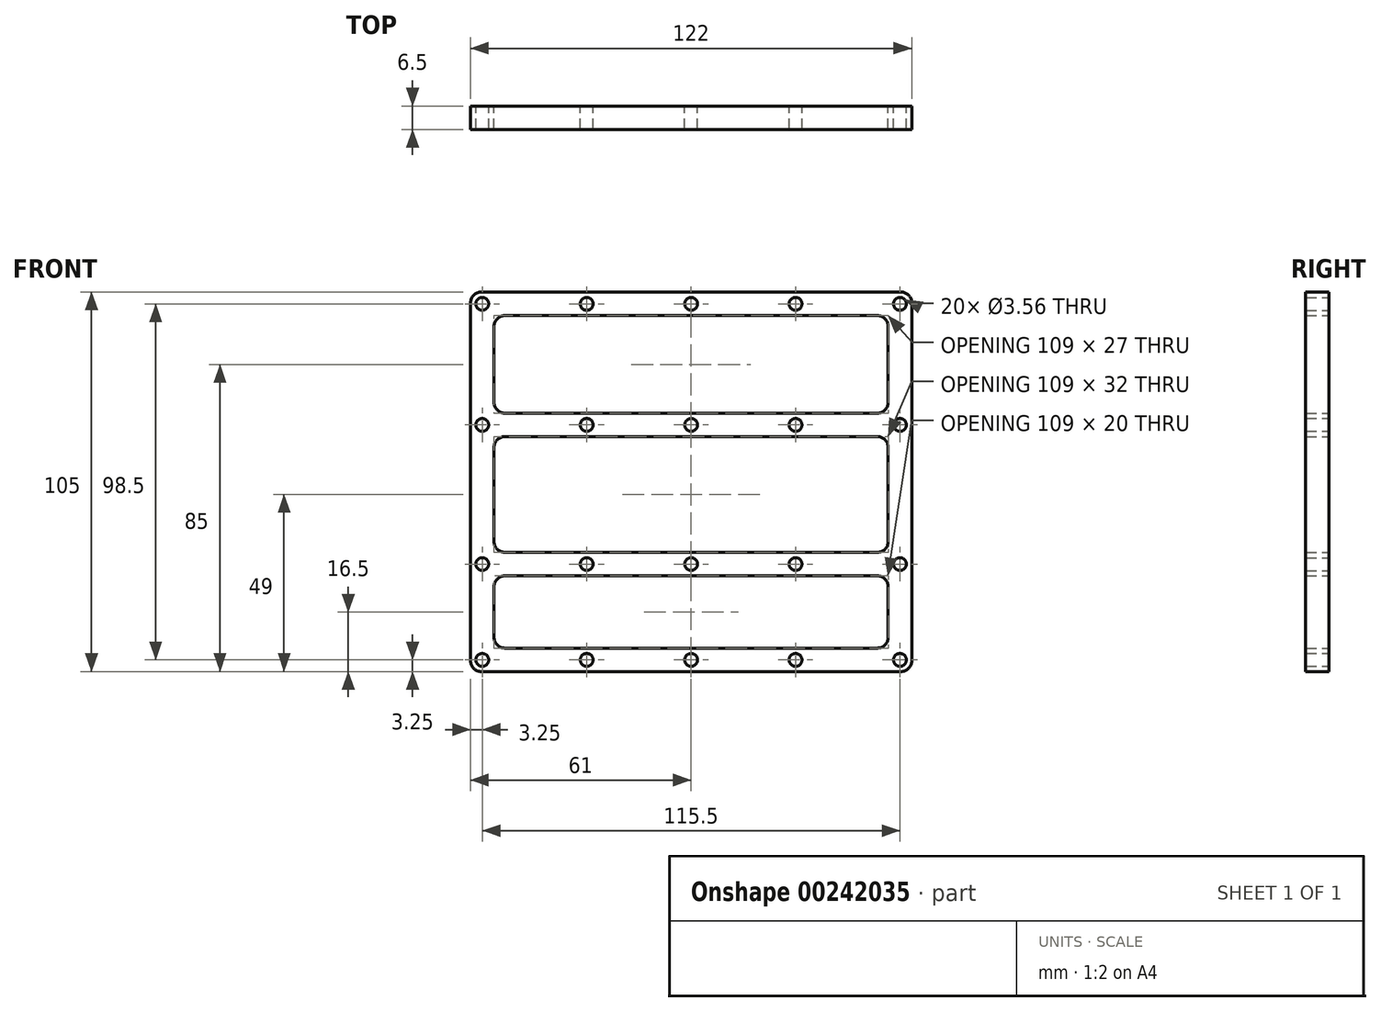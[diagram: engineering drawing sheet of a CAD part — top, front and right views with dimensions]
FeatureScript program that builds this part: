
annotation { "Feature Type Name" : "Feature", "Feature Type Description" : "" }
export const myFeature = defineFeature(function(context is Context, id is Id, definition is map)
    precondition{}
    {
        {
            var Q0;
            Q0=qCreatedBy(makeId("Front.planeOp"),FACE);
            var sketch = newSketch(context, id + "F0", { "sketchPlane" : qUnion([Q0])});
            skLineSegment(sketch, "E0", {"start": v(0, 3) * mm, "end": v(0, 102) * mm});
            skLineSegment(sketch, "E1", {"start": v(3, 105) * mm, "end": v(119, 105) * mm});
            skLineSegment(sketch, "E2", {"start": v(122, 102) * mm, "end": v(122, 3) * mm});
            skLineSegment(sketch, "E3", {"start": v(119, 0) * mm, "end": v(3, 0) * mm});
            skLineSegment(sketch, "E4", {"start": v(9.5, 6.5) * mm, "end": v(112.5, 6.5) * mm});
            skLineSegment(sketch, "E5", {"start": v(115.5, 9.5) * mm, "end": v(115.5, 23.5) * mm});
            skLineSegment(sketch, "E6", {"start": v(112.5, 26.5) * mm, "end": v(9.5, 26.5) * mm});
            skLineSegment(sketch, "E7", {"start": v(6.5, 23.5) * mm, "end": v(6.5, 9.5) * mm});
            skLineSegment(sketch, "E8", {"start": v(6.5, 36) * mm, "end": v(6.5, 62) * mm});
            skLineSegment(sketch, "E9", {"start": v(9.5, 65) * mm, "end": v(112.5, 65) * mm});
            skLineSegment(sketch, "E10", {"start": v(115.5, 62) * mm, "end": v(115.5, 36) * mm});
            skLineSegment(sketch, "E11", {"start": v(112.5, 33) * mm, "end": v(9.5, 33) * mm});
            skLineSegment(sketch, "E12", {"start": v(6.5, 95.5) * mm, "end": v(6.5, 74.5) * mm});
            skLineSegment(sketch, "E13", {"start": v(9.5, 71.5) * mm, "end": v(112.5, 71.5) * mm});
            skLineSegment(sketch, "E14", {"start": v(115.5, 74.5) * mm, "end": v(115.5, 95.5) * mm});
            skLineSegment(sketch, "E15", {"start": v(9.5, 98.5) * mm, "end": v(112.5, 98.5) * mm});
            skPoint(sketch, "E16.visualSharp", {"position": v(0, 105) * mm});
            skArc(sketch, "E16.filletArc", {"start": v(3, 105) * mm, "mid": v(0.88, 104.12) * mm, "end": v(0, 102) * mm});
            skPoint(sketch, "E17.visualSharp", {"position": v(6.5, 98.5) * mm});
            skArc(sketch, "E17.filletArc", {"start": v(9.5, 98.5) * mm, "mid": v(7.38, 97.62) * mm, "end": v(6.5, 95.5) * mm});
            skPoint(sketch, "E18.visualSharp", {"position": v(115.5, 98.5) * mm});
            skArc(sketch, "E18.filletArc", {"start": v(115.5, 95.5) * mm, "mid": v(114.62, 97.62) * mm, "end": v(112.5, 98.5) * mm});
            skPoint(sketch, "E19.visualSharp", {"position": v(122, 105) * mm});
            skArc(sketch, "E19.filletArc", {"start": v(122, 102) * mm, "mid": v(121.12, 104.12) * mm, "end": v(119, 105) * mm});
            skPoint(sketch, "E20.visualSharp", {"position": v(115.5, 71.5) * mm});
            skArc(sketch, "E20.filletArc", {"start": v(112.5, 71.5) * mm, "mid": v(114.62, 72.38) * mm, "end": v(115.5, 74.5) * mm});
            skPoint(sketch, "E21.visualSharp", {"position": v(6.5, 71.5) * mm});
            skArc(sketch, "E21.filletArc", {"start": v(6.5, 74.5) * mm, "mid": v(7.38, 72.38) * mm, "end": v(9.5, 71.5) * mm});
            skPoint(sketch, "E22.visualSharp", {"position": v(6.5, 65) * mm});
            skArc(sketch, "E22.filletArc", {"start": v(9.5, 65) * mm, "mid": v(7.38, 64.12) * mm, "end": v(6.5, 62) * mm});
            skPoint(sketch, "E23.visualSharp", {"position": v(115.5, 65) * mm});
            skArc(sketch, "E23.filletArc", {"start": v(115.5, 62) * mm, "mid": v(114.62, 64.12) * mm, "end": v(112.5, 65) * mm});
            skPoint(sketch, "E24.visualSharp", {"position": v(6.5, 33) * mm});
            skArc(sketch, "E24.filletArc", {"start": v(6.5, 36) * mm, "mid": v(7.38, 33.88) * mm, "end": v(9.5, 33) * mm});
            skPoint(sketch, "E25.visualSharp", {"position": v(115.5, 33) * mm});
            skArc(sketch, "E25.filletArc", {"start": v(112.5, 33) * mm, "mid": v(114.62, 33.88) * mm, "end": v(115.5, 36) * mm});
            skPoint(sketch, "E26.visualSharp", {"position": v(115.5, 26.5) * mm});
            skArc(sketch, "E26.filletArc", {"start": v(115.5, 23.5) * mm, "mid": v(114.62, 25.62) * mm, "end": v(112.5, 26.5) * mm});
            skPoint(sketch, "E27.visualSharp", {"position": v(6.5, 26.5) * mm});
            skArc(sketch, "E27.filletArc", {"start": v(9.5, 26.5) * mm, "mid": v(7.38, 25.62) * mm, "end": v(6.5, 23.5) * mm});
            skPoint(sketch, "E28.visualSharp", {"position": v(6.5, 6.5) * mm});
            skArc(sketch, "E28.filletArc", {"start": v(6.5, 9.5) * mm, "mid": v(7.38, 7.38) * mm, "end": v(9.5, 6.5) * mm});
            skPoint(sketch, "E29.visualSharp", {"position": v(115.5, 6.5) * mm});
            skArc(sketch, "E29.filletArc", {"start": v(112.5, 6.5) * mm, "mid": v(114.62, 7.38) * mm, "end": v(115.5, 9.5) * mm});
            skPoint(sketch, "E30.visualSharp", {"position": v(122, 0) * mm});
            skArc(sketch, "E30.filletArc", {"start": v(119, 0) * mm, "mid": v(121.12, 0.88) * mm, "end": v(122, 3) * mm});
            skPoint(sketch, "E31.visualSharp", {"position": v(0, 0) * mm});
            skArc(sketch, "E31.filletArc", {"start": v(0, 3) * mm, "mid": v(0.88, 0.88) * mm, "end": v(3, 0) * mm});
            skLineSegment(sketch, "E32", {"start": v(0, 52.5) * mm, "end": v(6.5, 52.5) * mm, "construction": true});
            skLineSegment(sketch, "E33", {"start": v(3.25, 52.5) * mm, "end": v(3.25, 18.78) * mm, "construction": true});
            skLineSegment(sketch, "E34", {"start": v(31.26, 33) * mm, "end": v(31.26, 26.5) * mm, "construction": true});
            skLineSegment(sketch, "E35", {"start": v(31.26, 29.75) * mm, "end": v(-5.9, 29.75) * mm, "construction": true});
            skPoint(sketch, "E36", {"position": v(3.25, 29.75) * mm});
            skCircle(sketch, "E37", {"center": v(3.25, 29.75) * mm, "radius": 1.78 * mm});
            skCircle(sketch, "E38.0.1.0", {"center": v(3.25, 68.25) * mm, "radius": 1.78 * mm});
            skLineSegment(sketch, "E38.direction1", {"start": v(3.25, 29.75) * mm, "end": v(28.25, 29.75) * mm, "construction": true});
            skLineSegment(sketch, "E38.direction2", {"start": v(3.25, 29.75) * mm, "end": v(3.25, 68.25) * mm, "construction": true});
            skCircle(sketch, "E39.0.1.0", {"center": v(3.25, 101.75) * mm, "radius": 1.78 * mm});
            skLineSegment(sketch, "E39.direction1", {"start": v(3.25, 68.25) * mm, "end": v(28.25, 68.25) * mm, "construction": true});
            skLineSegment(sketch, "E39.direction2", {"start": v(3.25, 68.25) * mm, "end": v(3.25, 101.75) * mm, "construction": true});
            skCircle(sketch, "E40.0.1.0", {"center": v(3.25, 3.25) * mm, "radius": 1.78 * mm});
            skLineSegment(sketch, "E40.direction2", {"start": v(3.25, 29.75) * mm, "end": v(3.25, 3.25) * mm, "construction": true});
            skCircle(sketch, "E41.1.0.0", {"center": v(32.12, 101.75) * mm, "radius": 1.78 * mm});
            skCircle(sketch, "E41.1.0.1", {"center": v(32.12, 68.25) * mm, "radius": 1.78 * mm});
            skCircle(sketch, "E41.1.0.2", {"center": v(32.12, 29.75) * mm, "radius": 1.78 * mm});
            skCircle(sketch, "E41.1.0.3", {"center": v(32.12, 3.25) * mm, "radius": 1.78 * mm});
            skCircle(sketch, "E41.2.0.0", {"center": v(61, 101.75) * mm, "radius": 1.78 * mm});
            skCircle(sketch, "E41.2.0.1", {"center": v(61, 68.25) * mm, "radius": 1.78 * mm});
            skCircle(sketch, "E41.2.0.2", {"center": v(61, 29.75) * mm, "radius": 1.78 * mm});
            skCircle(sketch, "E41.2.0.3", {"center": v(61, 3.25) * mm, "radius": 1.78 * mm});
            skCircle(sketch, "E41.3.0.0", {"center": v(89.88, 101.75) * mm, "radius": 1.78 * mm});
            skCircle(sketch, "E41.3.0.1", {"center": v(89.88, 68.25) * mm, "radius": 1.78 * mm});
            skCircle(sketch, "E41.3.0.2", {"center": v(89.88, 29.75) * mm, "radius": 1.78 * mm});
            skCircle(sketch, "E41.3.0.3", {"center": v(89.88, 3.25) * mm, "radius": 1.78 * mm});
            skCircle(sketch, "E41.4.0.0", {"center": v(118.75, 101.75) * mm, "radius": 1.78 * mm});
            skCircle(sketch, "E41.4.0.1", {"center": v(118.75, 68.25) * mm, "radius": 1.78 * mm});
            skCircle(sketch, "E41.4.0.2", {"center": v(118.75, 29.75) * mm, "radius": 1.78 * mm});
            skCircle(sketch, "E41.4.0.3", {"center": v(118.75, 3.25) * mm, "radius": 1.78 * mm});
            skLineSegment(sketch, "E41.direction1", {"start": v(3.25, 101.75) * mm, "end": v(32.12, 101.75) * mm, "construction": true});
            skSolve(sketch);
        }
        {
            var Q0;
            Q0 = qSketchRegion(id + "F0", true);
            extrude(context, id + "F1", {"entities" : qUnion([Q0]), "depth" : 6.5 * mm});
        }
    });
